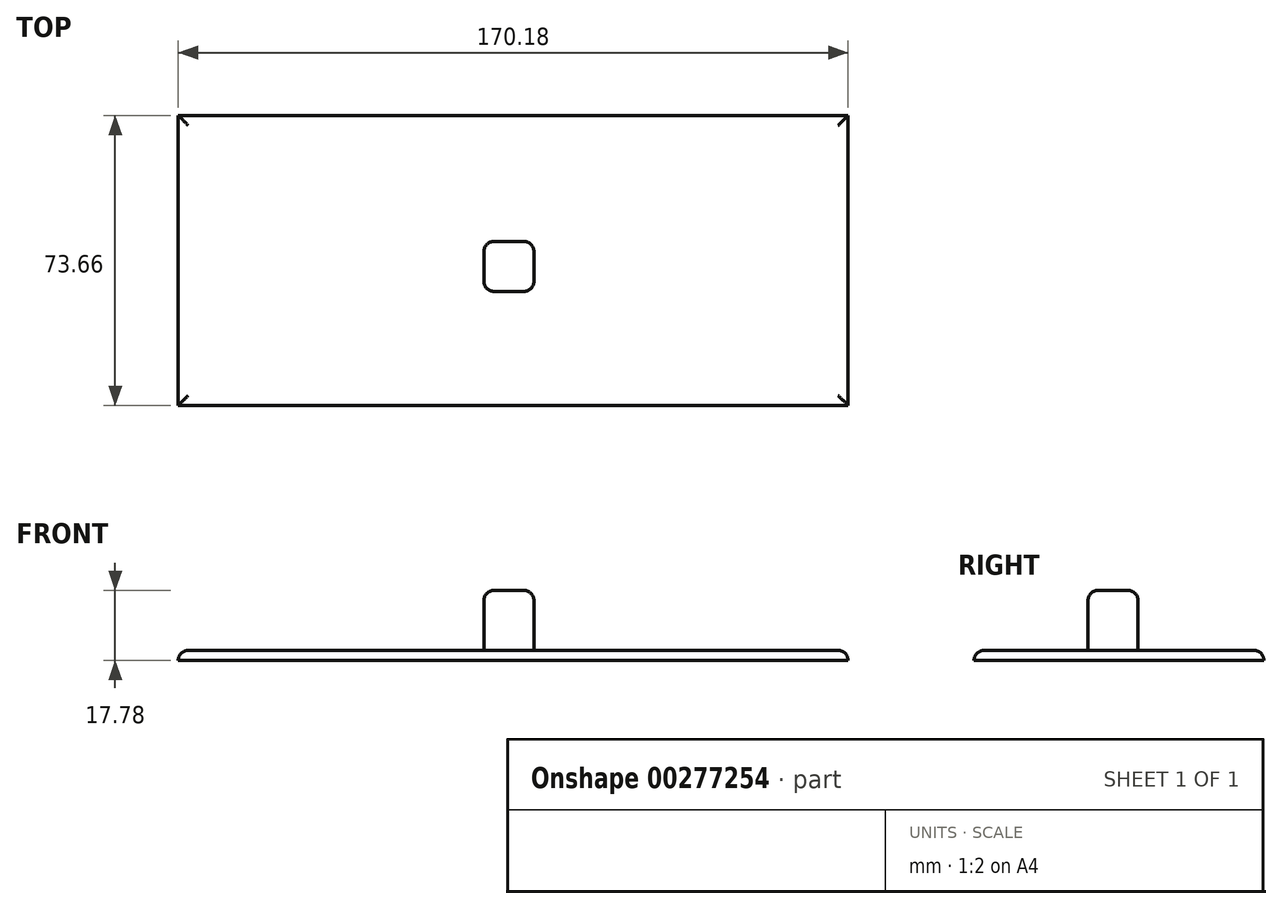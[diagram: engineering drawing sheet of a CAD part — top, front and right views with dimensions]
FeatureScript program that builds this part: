
annotation { "Feature Type Name" : "Feature", "Feature Type Description" : "" }
export const myFeature = defineFeature(function(context is Context, id is Id, definition is map)
    precondition{}
    {
        {
            var Q0;
            Q0=qCreatedBy(makeId("Top.planeOp"),FACE);
            var sketch = newSketch(context, id + "F0", { "sketchPlane" : qUnion([Q0])});
            skLineSegment(sketch, "E0.bottom", {"start": v(-84.01, -36.83) * mm, "end": v(86.17, -36.83) * mm});
            skLineSegment(sketch, "E0.top", {"start": v(-84.01, 36.83) * mm, "end": v(86.17, 36.83) * mm});
            skLineSegment(sketch, "E0.left", {"start": v(-84.01, -36.83) * mm, "end": v(-84.01, 36.83) * mm});
            skLineSegment(sketch, "E0.right", {"start": v(86.17, -36.83) * mm, "end": v(86.17, 36.83) * mm});
            skPoint(sketch, "E0.middle", {"position": v(1.08, 0) * mm});
            skSolve(sketch);
        }
        {
            var Q0;
            Q0 = qSketchRegion(id + "F0", true);
            extrude(context, id + "F1", {"entities" : qUnion([Q0]), "depth" : 2.54 * mm, "offsetDistance" : 25.4 * mm});
        }
        {
            var Q0;
            Q0=makeQuery(id+"F1.opExtrude","CAP_FACE",FACE,{"disambiguationData":[OSD([sQuery(id+"F0.wireOp",EDGE,"E0.bottom"),sQuery(id+"F0.wireOp",EDGE,"E0.top"),sQuery(id+"F0.wireOp",EDGE,"E0.left"),sQuery(id+"F0.wireOp",EDGE,"E0.right")])],"isStart":false});
            var sketch = newSketch(context, id + "F2", { "sketchPlane" : qUnion([Q0])});
            skLineSegment(sketch, "E1.bottom", {"start": v(-6.35, -7.87) * mm, "end": v(6.35, -7.87) * mm});
            skLineSegment(sketch, "E1.top", {"start": v(-6.35, 4.83) * mm, "end": v(6.35, 4.83) * mm});
            skLineSegment(sketch, "E1.left", {"start": v(-6.35, -7.87) * mm, "end": v(-6.35, 4.83) * mm});
            skLineSegment(sketch, "E1.right", {"start": v(6.35, -7.87) * mm, "end": v(6.35, 4.83) * mm});
            skPoint(sketch, "E1.middle", {"position": v(0, -1.52) * mm});
            skSolve(sketch);
        }
        {
            var Q0;
            Q0 = qSketchRegion(id + "F2", true);
            extrude(context, id + "F3", {"entities" : qUnion([Q0]), "operationType" : NewBodyOperationType.ADD, "depth" : 15.24 * mm, "offsetDistance" : 25.4 * mm});
        }
        {
            var Q0;
            Q0=makeQuery(id+"F3.opExtrude","CAP_EDGE",EDGE,{"disambiguationData":[OSD([sQuery(id+"F2.wireOp",EDGE,"E1.bottom")])],"isStart":false});
            var Q1;
            Q1=makeQuery(id+"F3.opExtrude","CAP_EDGE",EDGE,{"disambiguationData":[OSD([sQuery(id+"F2.wireOp",EDGE,"E1.left")])],"isStart":false});
            var Q2;
            Q2=makeQuery(id+"F3.opExtrude","CAP_EDGE",EDGE,{"disambiguationData":[OSD([sQuery(id+"F2.wireOp",EDGE,"E1.top")])],"isStart":false});
            var Q3;
            Q3=makeQuery(id+"F3.opExtrude","CAP_EDGE",EDGE,{"disambiguationData":[OSD([sQuery(id+"F2.wireOp",EDGE,"E1.right")])],"isStart":false});
            var Q4;
            Q4=makeQuery(id+"F3.opExtrude","SWEPT_EDGE",EDGE,{"disambiguationData":[OSD([sQuery(id+"F2.wireOp",EDGE,"E1.bottom"),sQuery(id+"F2.wireOp",EDGE,"E1.left")])]});
            var Q5;
            Q5=makeQuery(id+"F3.opExtrude","SWEPT_EDGE",EDGE,{"disambiguationData":[OSD([sQuery(id+"F2.wireOp",EDGE,"E1.bottom"),sQuery(id+"F2.wireOp",EDGE,"E1.right")])]});
            var Q6;
            Q6=makeQuery(id+"F3.opExtrude","SWEPT_EDGE",EDGE,{"disambiguationData":[OSD([sQuery(id+"F2.wireOp",EDGE,"E1.top"),sQuery(id+"F2.wireOp",EDGE,"E1.right")])]});
            var Q7;
            Q7=makeQuery(id+"F3.opExtrude","SWEPT_EDGE",EDGE,{"disambiguationData":[OSD([sQuery(id+"F2.wireOp",EDGE,"E1.top"),sQuery(id+"F2.wireOp",EDGE,"E1.left")])]});
            var Q8;
            Q8=makeQuery(id+"F1.opExtrude","CAP_EDGE",EDGE,{"disambiguationData":[OSD([sQuery(id+"F0.wireOp",EDGE,"E0.bottom")])],"isStart":false});
            var Q9;
            Q9=makeQuery(id+"F1.opExtrude","CAP_EDGE",EDGE,{"disambiguationData":[OSD([sQuery(id+"F0.wireOp",EDGE,"E0.right")])],"isStart":false});
            var Q10;
            Q10=makeQuery(id+"F1.opExtrude","CAP_EDGE",EDGE,{"disambiguationData":[OSD([sQuery(id+"F0.wireOp",EDGE,"E0.top")])],"isStart":false});
            var Q11;
            Q11=makeQuery(id+"F1.opExtrude","CAP_EDGE",EDGE,{"disambiguationData":[OSD([sQuery(id+"F0.wireOp",EDGE,"E0.left")])],"isStart":false});
            fillet(context, id + "F4", {"entities" : qUnion([Q0, Q1, Q2, Q3, Q4, Q5, Q6, Q7, Q8, Q9, Q10, Q11]), "radius" : 2.54 * mm, "tangentPropagation" : true, "allowEdgeOverflow" : false});
        }
    });
